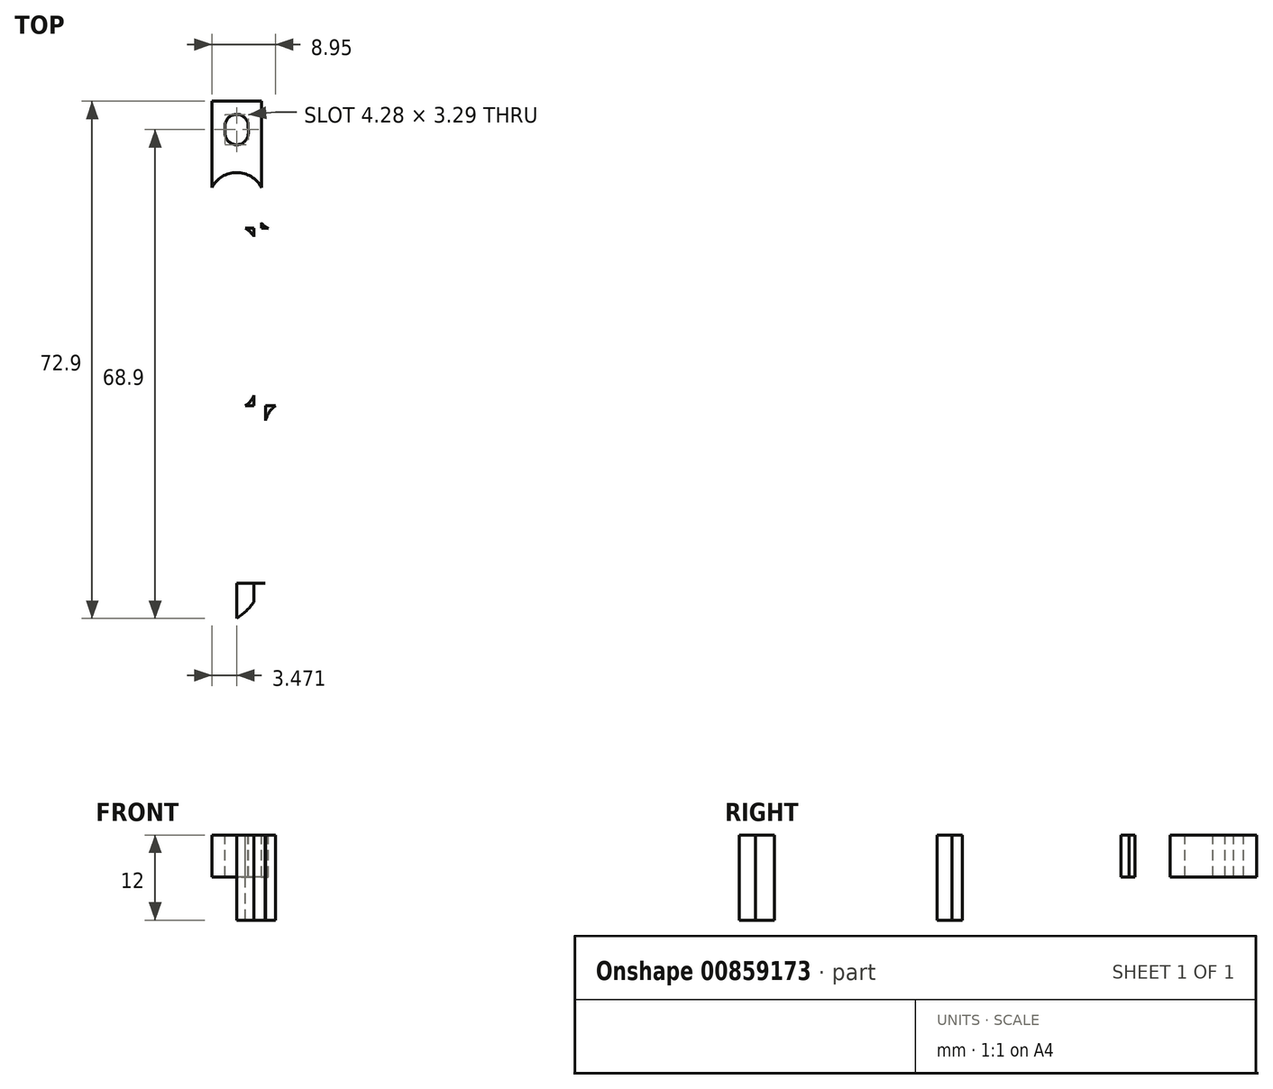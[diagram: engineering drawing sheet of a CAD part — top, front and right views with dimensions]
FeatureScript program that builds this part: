
annotation { "Feature Type Name" : "Feature", "Feature Type Description" : "" }
export const myFeature = defineFeature(function(context is Context, id is Id, definition is map)
    precondition{}
    {
        {
            var Q0;
            Q0=qCreatedBy(makeId("Top.planeOp"),FACE);
            var sketch = newSketch(context, id + "F0", { "sketchPlane" : qUnion([Q0])});
            skLineSegment(sketch, "E0.bottom", {"start": v(0, 0) * mm, "end": v(6.95, 0) * mm});
            skLineSegment(sketch, "E0.top", {"start": v(0, 17.9) * mm, "end": v(6.95, 17.9) * mm});
            skLineSegment(sketch, "E0.left", {"start": v(0, 0) * mm, "end": v(0, 17.9) * mm});
            skLineSegment(sketch, "E0.right", {"start": v(6.95, 0) * mm, "end": v(6.95, 17.9) * mm});
            skLineSegment(sketch, "E1", {"start": v(0, 0) * mm, "end": v(0, 7.85) * mm});
            skLineSegment(sketch, "E2", {"start": v(3.48, 0) * mm, "end": v(3.48, 7.85) * mm});
            skLineSegment(sketch, "E3", {"start": v(3.48, 7.85) * mm, "end": v(3.48, 6.9) * mm});
            skCircle(sketch, "E4", {"center": v(3.48, 3.92) * mm, "radius": 3.92 * mm});
            skLineSegment(sketch, "E5", {"start": v(3.47, 17.9) * mm, "end": v(3.47, 16.05) * mm});
            skLineSegment(sketch, "E6", {"start": v(3.47, 16.05) * mm, "end": v(3.48, 11.75) * mm});
            skLineSegment(sketch, "E7", {"start": v(3.47, 13.9) * mm, "end": v(3.47, 16.05) * mm});
            skLineSegment(sketch, "E8", {"start": v(3.48, 11.75) * mm, "end": v(3.47, 13.9) * mm});
            skLineSegment(sketch, "E9", {"start": v(4.55, 12.83) * mm, "end": v(4.55, 14.98) * mm});
            skLineSegment(sketch, "E10.bottom", {"start": v(3.48, 0) * mm, "end": v(1.03, 0) * mm});
            skLineSegment(sketch, "E10.top", {"start": v(3.48, -100) * mm, "end": v(1.03, -100) * mm});
            skLineSegment(sketch, "E10.left", {"start": v(3.48, 0) * mm, "end": v(3.48, -100) * mm});
            skLineSegment(sketch, "E10.right", {"start": v(1.03, 0) * mm, "end": v(1.03, -100) * mm});
            skLineSegment(sketch, "E11.bottom", {"start": v(3.48, 0) * mm, "end": v(5.93, 0) * mm});
            skLineSegment(sketch, "E11.top", {"start": v(3.48, -100) * mm, "end": v(5.93, -100) * mm});
            skLineSegment(sketch, "E11.right", {"start": v(5.93, 0) * mm, "end": v(5.93, -100) * mm});
            skLineSegment(sketch, "E12", {"start": v(5.93, 0) * mm, "end": v(5.93, 1.16) * mm});
            skLineSegment(sketch, "E13", {"start": v(1.03, 0) * mm, "end": v(1.02, 1.22) * mm});
            skLineSegment(sketch, "E14.bottom", {"start": v(6.95, 0) * mm, "end": v(9.83, -0.08) * mm});
            skLineSegment(sketch, "E14.left", {"start": v(6.95, 0) * mm, "end": v(6.95, 1.5) * mm});
            skLineSegment(sketch, "E15.right", {"start": v(5.93, -0.08) * mm, "end": v(5.93, -100) * mm});
            skLineSegment(sketch, "E16", {"start": v(3.48, 0) * mm, "end": v(3.48, -12.11) * mm});
            skLineSegment(sketch, "E17", {"start": v(3.48, 0) * mm, "end": v(3.48, -25) * mm});
            skLineSegment(sketch, "E18", {"start": v(3.48, -25) * mm, "end": v(1.03, -25) * mm});
            skLineSegment(sketch, "E19", {"start": v(1.03, -25) * mm, "end": v(1.03, -25.71) * mm});
            skLineSegment(sketch, "E20", {"start": v(1.03, -25) * mm, "end": v(1.03, -30) * mm});
            skLineSegment(sketch, "E21", {"start": v(5.93, -25) * mm, "end": v(5.93, -50) * mm});
            skPoint(sketch, "E21.startSnap0", {"position": v(2.25, -25) * mm});
            skLineSegment(sketch, "E22", {"start": v(5.93, -50) * mm, "end": v(9.83, -50.04) * mm});
            skLineSegment(sketch, "E23", {"start": v(3.48, -50) * mm, "end": v(1.03, -50) * mm});
            skLineSegment(sketch, "E24", {"start": v(5.93, -25) * mm, "end": v(9.83, -25) * mm});
            skLineSegment(sketch, "E25", {"start": v(5.93, -25) * mm, "end": v(5.93, -21.38) * mm});
            skLineSegment(sketch, "E26", {"start": v(5.93, -25) * mm, "end": v(5.93, -22.99) * mm});
            skLineSegment(sketch, "E27", {"start": v(3.48, -25) * mm, "end": v(3.48, -26.23) * mm});
            skLineSegment(sketch, "E28", {"start": v(5.93, -50) * mm, "end": v(5.93, -52.01) * mm});
            skLineSegment(sketch, "E29", {"start": v(3.48, -50) * mm, "end": v(3.48, -48.78) * mm});
            skLineSegment(sketch, "E30", {"start": v(5.93, -25) * mm, "end": v(5.93, -26.95) * mm});
            skLineSegment(sketch, "E31", {"start": v(3.48, -50) * mm, "end": v(5.93, -50) * mm});
            skLineSegment(sketch, "E32", {"start": v(3.48, 0) * mm, "end": v(3.48, -1.23) * mm});
            skLineSegment(sketch, "E33", {"start": v(6.95, 0) * mm, "end": v(6.95, 1.44) * mm});
            skLineSegment(sketch, "E34", {"start": v(1.03, 0) * mm, "end": v(1.03, -0.69) * mm});
            skLineSegment(sketch, "E35", {"start": v(1.03, 0) * mm, "end": v(1.03, -1) * mm});
            skLineSegment(sketch, "E36", {"start": v(5.92, 0) * mm, "end": v(5.92, -1.23) * mm});
            skFitSpline(sketch, "E37", {"points": [v(4.7, 0) * mm, v(5.92, -1.23) * mm], "startDerivative": vector(1.66, -0.95) * mm, "endDerivative": vector(0.86, -1.52) * mm});
            skLineSegment(sketch, "E38", {"start": v(5.93, -25) * mm, "end": v(5.93, -28.9) * mm});
            skLineSegment(sketch, "E39", {"start": v(3.48, -25) * mm, "end": v(5.93, -25) * mm});
            skLineSegment(sketch, "E40", {"start": v(5.93, -25) * mm, "end": v(5.93, -22.55) * mm});
            skLineSegment(sketch, "E41", {"start": v(5.93, -50) * mm, "end": v(5.93, -47.55) * mm});
            skLineSegment(sketch, "E42.left", {"start": v(5.93, -50) * mm, "end": v(5.93, -100) * mm});
            skLineSegment(sketch, "E43", {"start": v(9.83, -0.08) * mm, "end": v(9.83, -50.04) * mm});
            skLineSegment(sketch, "E44.bottom", {"start": v(9.83, -0.08) * mm, "end": v(12.2, -0.08) * mm});
            skLineSegment(sketch, "E44.top", {"start": v(9.83, -50.08) * mm, "end": v(12.2, -50.08) * mm});
            skLineSegment(sketch, "E44.left", {"start": v(9.83, -0.08) * mm, "end": v(9.83, -50.08) * mm});
            skLineSegment(sketch, "E44.right", {"start": v(12.2, -0.08) * mm, "end": v(12.2, -50.08) * mm});
            skLineSegment(sketch, "E45.bottom", {"start": v(5.93, -50) * mm, "end": v(8.3, -50) * mm});
            skLineSegment(sketch, "E45.top", {"start": v(5.93, -100) * mm, "end": v(8.3, -100) * mm});
            skLineSegment(sketch, "E45.right", {"start": v(8.3, -50) * mm, "end": v(8.3, -100) * mm});
            skLineSegment(sketch, "E46", {"start": v(8.3, -50) * mm, "end": v(12.2, -50.08) * mm});
            skLineSegment(sketch, "E47", {"start": v(8.3, -50) * mm, "end": v(8.3, -53.9) * mm});
            skFitSpline(sketch, "E48", {"points": [v(8.3, -53.9) * mm, v(10.24, -50.04) * mm], "startDerivative": vector(0.85, 4.55) * mm, "endDerivative": vector(3.1, 3.55) * mm});
            skLineSegment(sketch, "E49", {"start": v(3.47, 13.9) * mm, "end": v(3.47, 12.9) * mm});
            skLineSegment(sketch, "E50", {"start": v(3.47, 13.9) * mm, "end": v(3.47, 14.9) * mm});
            skCircle(sketch, "E51", {"center": v(3.47, 13.4) * mm, "radius": 1.64 * mm});
            skArc(sketch, "E52", {"start": v(5.1, 14.7) * mm, "mid": v(1.83, 14.37) * mm, "end": v(5.1, 14.14) * mm});
            skLineSegment(sketch, "E53", {"start": v(3.48, 11.75) * mm, "end": v(1.27, 11.75) * mm});
            skLineSegment(sketch, "E54", {"start": v(3.48, 11.75) * mm, "end": v(5.93, 11.75) * mm});
            skLineSegment(sketch, "E55", {"start": v(3.47, 16.05) * mm, "end": v(1.21, 16.05) * mm});
            skLineSegment(sketch, "E56", {"start": v(3.47, 16.05) * mm, "end": v(5.69, 16.05) * mm});
            skLineSegment(sketch, "E57", {"start": v(5.11, 13.43) * mm, "end": v(5.1, 14.7) * mm});
            skLineSegment(sketch, "E58", {"start": v(1.84, 13.46) * mm, "end": v(1.83, 14.38) * mm});
            skLineSegment(sketch, "E59", {"start": v(9.83, -25) * mm, "end": v(12.2, -25) * mm});
            skFitSpline(sketch, "E60", {"points": [v(11.01, -0.08) * mm, v(12.2, -1.97) * mm], "startDerivative": vector(2.1, -1.32) * mm, "endDerivative": vector(0, -2.03) * mm});
            skLineSegment(sketch, "E61", {"start": v(5.93, -25) * mm, "end": v(5.93, -43) * mm});
            skLineSegment(sketch, "E62", {"start": v(5.93, -43) * mm, "end": v(9.83, -43) * mm});
            skLineSegment(sketch, "E63", {"start": v(6.95, 0) * mm, "end": v(8.95, -0.06) * mm});
            skLineSegment(sketch, "E64", {"start": v(8.95, -0.06) * mm, "end": v(8.95, -25) * mm});
            skLineSegment(sketch, "E65", {"start": v(6.95, 0) * mm, "end": v(7.95, -0.03) * mm});
            skFitSpline(sketch, "E66", {"points": [v(7.95, -0.03) * mm, v(6.95, 0.75) * mm], "startDerivative": vector(-1.3, 0.67) * mm, "endDerivative": vector(-0.63, 0.9) * mm});
            skFitSpline(sketch, "E67", {"points": [v(7.95, -0.03) * mm, v(8.95, -1) * mm], "startDerivative": vector(1.44, -0.65) * mm, "endDerivative": vector(0.55, -1.15) * mm});
            skLineSegment(sketch, "E68", {"start": v(5.93, -25) * mm, "end": v(7.53, -25) * mm});
            skLineSegment(sketch, "E69", {"start": v(7.53, -25) * mm, "end": v(7.53, -43) * mm});
            skPoint(sketch, "E69.endSnap0", {"position": v(7.88, -43) * mm});
            skFitSpline(sketch, "E70", {"points": [v(8.95, -25) * mm, v(7.53, -27.1) * mm], "startDerivative": vector(-2.11, -1.57) * mm, "endDerivative": vector(-1.16, -3.2) * mm});
            skCircle(sketch, "E71", {"center": v(3.48, 3.92) * mm, "radius": 2.77 * mm});
            skFitSpline(sketch, "E72", {"points": [v(4.7, -25) * mm, v(5.93, -23.52) * mm], "startDerivative": vector(1.9, 1.19) * mm, "endDerivative": vector(0.85, 2) * mm});
            skFitSpline(sketch, "E73", {"points": [v(4.7, -25) * mm, v(3.48, -26.23) * mm], "startDerivative": vector(-1.92, -0.79) * mm, "endDerivative": vector(-0.51, -1.86) * mm});
            skLineSegment(sketch, "E74", {"start": v(7.53, -43) * mm, "end": v(7.45, -50.02) * mm});
            skLineSegment(sketch, "E75", {"start": v(3.48, -50) * mm, "end": v(3.48, -55) * mm});
            skLineSegment(sketch, "E76", {"start": v(3.48, -55) * mm, "end": v(7.45, -55) * mm});
            skLineSegment(sketch, "E77", {"start": v(7.45, -55) * mm, "end": v(7.45, -50.02) * mm});
            skFitSpline(sketch, "E78", {"points": [v(3.48, -55) * mm, v(7.45, -50.02) * mm], "startDerivative": vector(6.1, 4.07) * mm, "endDerivative": vector(2.72, 5.79) * mm});
            skSolve(sketch);
        }
        {
            var Q0;
            {var subQ0=sQuery(id+"F0.wireOp",EDGE,"E4");var subQ3=sQuery(id+"F0.wireOp",EDGE,"E0.right");var subQ10=makeQuery(id+"F0.imprint","INTERSECT",VERTEX,{"disambiguationData":[OD(0.0)],"derivedFrom":[subQ3,subQ0]});Q0=makeQuery(id+"F0.imprint","IMPRINT",FACE,{"disambiguationData":[TD([[makeQuery(id+"F0.imprint","IMPRINT",EDGE,{"disambiguationData":[TD([[subQ10,-1.0]])],"derivedFrom":subQ3}),1.0]])]});}
            var Q1;
            {var subQ0=sQuery(id+"F0.wireOp",EDGE,"E4");var subQ7=sQuery(id+"F0.wireOp",EDGE,"E1");var subQ10=makeQuery(id+"F0.imprint","INTERSECT",VERTEX,{"disambiguationData":[OD(0.0)],"derivedFrom":[subQ7,subQ0]});Q1=makeQuery(id+"F0.imprint","IMPRINT",FACE,{"disambiguationData":[TD([[makeQuery(id+"F0.imprint","IMPRINT",EDGE,{"disambiguationData":[TD([[subQ10,-1.0]])],"derivedFrom":subQ7}),-1.0]])]});}
            var Q2;
            {var subQ0=sQuery(id+"F0.wireOp",EDGE,"E1");var subQ1=sQuery(id+"F0.wireOp",EDGE,"E0.bottom");var subQ2=makeQuery(id+"F0.imprint","INTERSECT",VERTEX,{"derivedFrom":[subQ1,subQ0]});Q2=makeQuery(id+"F0.imprint","IMPRINT",FACE,{"disambiguationData":[TD([[makeQuery(id+"F0.imprint","IMPRINT",EDGE,{"disambiguationData":[TD([[subQ2,-1.0]])],"derivedFrom":subQ0}),-1.0]])]});}
            var Q3;
            {var subQ0=sQuery(id+"F0.wireOp",EDGE,"E10.bottom");Q3=makeQuery(id+"F0.imprint","IMPRINT",FACE,{"disambiguationData":[TD([[makeQuery(id+"F0.imprint","IMPRINT",EDGE,{"derivedFrom":subQ0}),-1.0]])]});}
            var Q4;
            {var subQ0=sQuery(id+"F0.wireOp",EDGE,"E4");var subQ1=sQuery(id+"F0.wireOp",EDGE,"E1");var subQ2=makeQuery(id+"F0.imprint","INTERSECT",VERTEX,{"disambiguationData":[OD(0.0)],"derivedFrom":[subQ1,subQ0]});Q4=makeQuery(id+"F0.imprint","IMPRINT",FACE,{"disambiguationData":[TD([[makeQuery(id+"F0.imprint","IMPRINT",EDGE,{"disambiguationData":[TD([[subQ2,-1.0]])],"derivedFrom":subQ1}),1.0]])]});}
            var Q5;
            {var subQ0=sQuery(id+"F0.wireOp",EDGE,"E4");var subQ1=sQuery(id+"F0.wireOp",EDGE,"E0.right");var subQ2=makeQuery(id+"F0.imprint","INTERSECT",VERTEX,{"disambiguationData":[OD(0.0)],"derivedFrom":[subQ1,subQ0]});Q5=makeQuery(id+"F0.imprint","IMPRINT",FACE,{"disambiguationData":[TD([[makeQuery(id+"F0.imprint","IMPRINT",EDGE,{"disambiguationData":[TD([[subQ2,-1.0]])],"derivedFrom":subQ1}),-1.0]])]});}
            var Q6;
            {var subQ5=sQuery(id+"F0.wireOp",EDGE,"E14.left");Q6=makeQuery(id+"F0.imprint","IMPRINT",FACE,{"disambiguationData":[TD([[makeQuery(id+"F0.imprint","IMPRINT",EDGE,{"derivedFrom":subQ5}),1.0]])]});}
            var Q7;
            {var subQ0=sQuery(id+"F0.wireOp",EDGE,"E11.bottom");var subQ5=makeQuery(id+"F0.imprint","INTERSECT",VERTEX,{"derivedFrom":[subQ0,sQuery(id+"F0.wireOp",EDGE,"E37")]});Q7=makeQuery(id+"F0.imprint","IMPRINT",FACE,{"disambiguationData":[TD([[makeQuery(id+"F0.imprint","IMPRINT",EDGE,{"disambiguationData":[TD([[subQ5,-1.0]])],"derivedFrom":subQ0}),1.0]])]});}
            var Q8;
            {var subQ3=sQuery(id+"F0.wireOp",EDGE,"E37");Q8=makeQuery(id+"F0.imprint","IMPRINT",FACE,{"disambiguationData":[TD([[makeQuery(id+"F0.imprint","IMPRINT",EDGE,{"derivedFrom":subQ3}),1.0]])]});}
            var Q9;
            Q9=makeQuery(id+"F0.imprint","IMPRINT",FACE,{"disambiguationData":[TD([[makeQuery(id+"F0.imprint","IMPRINT",EDGE,{"derivedFrom":sQuery(id+"F0.wireOp",EDGE,"E14.bottom")}),1.0]])]});
            extrude(context, id + "F1", {"entities" : qUnion([Q0, Q1, Q2, Q3, Q4, Q5, Q6, Q7, Q8, Q9]), "depth" : -5.9 * mm, "offsetDistance" : 25 * mm});
        }
        {
            var Q0;
            {var subQ15=sQuery(id+"F0.wireOp",EDGE,"E0.left");Q0=makeQuery(id+"F0.imprint","IMPRINT",FACE,{"disambiguationData":[TD([[makeQuery(id+"F0.imprint","IMPRINT",EDGE,{"derivedFrom":subQ15}),-1.0]])]});}
            extrude(context, id + "F2", {"entities" : qUnion([Q0]), "operationType" : NewBodyOperationType.ADD, "depth" : -2.5 * mm, "offsetDistance" : 25 * mm});
        }
        {
            var Q0;
            {var subQ5=sQuery(id+"F0.wireOp",EDGE,"E31");Q0=makeQuery(id+"F0.imprint","IMPRINT",FACE,{"disambiguationData":[TD([[makeQuery(id+"F0.imprint","IMPRINT",EDGE,{"derivedFrom":subQ5}),-1.0]])]});}
            var Q1;
            {var subQ0=sQuery(id+"F0.wireOp",EDGE,"E42.left");var subQ5=makeQuery(id+"F0.imprint","IMPRINT",VERTEX,{"derivedFrom":subQ0});Q1=makeQuery(id+"F0.imprint","IMPRINT",FACE,{"disambiguationData":[TD([[makeQuery(id+"F0.imprint","IMPRINT",EDGE,{"disambiguationData":[TD([[subQ5,-1.0]])],"derivedFrom":subQ0}),1.0]])]});}
            var Q2;
            {var subQ6=sQuery(id+"F0.wireOp",EDGE,"E21");Q2=makeQuery(id+"F0.imprint","IMPRINT",FACE,{"disambiguationData":[TD([[makeQuery(id+"F0.imprint","IMPRINT",EDGE,{"derivedFrom":subQ6}),1.0]])]});}
            var Q3;
            {var subQ6=sQuery(id+"F0.wireOp",EDGE,"E21");Q3=makeQuery(id+"F0.imprint","IMPRINT",FACE,{"disambiguationData":[TD([[makeQuery(id+"F0.imprint","IMPRINT",EDGE,{"derivedFrom":subQ6}),-1.0]])]});}
            var Q4;
            {var subQ8=sQuery(id+"F0.wireOp",EDGE,"E68");Q4=makeQuery(id+"F0.imprint","IMPRINT",FACE,{"disambiguationData":[TD([[makeQuery(id+"F0.imprint","IMPRINT",EDGE,{"derivedFrom":subQ8}),-1.0]])]});}
            var Q5;
            {var subQ4=sQuery(id+"F0.wireOp",EDGE,"E15.right");Q5=makeQuery(id+"F0.imprint","IMPRINT",FACE,{"disambiguationData":[TD([[makeQuery(id+"F0.imprint","IMPRINT",EDGE,{"derivedFrom":subQ4}),1.0]])]});}
            var Q6;
            {var subQ3=sQuery(id+"F0.wireOp",EDGE,"E72");Q6=makeQuery(id+"F0.imprint","IMPRINT",FACE,{"disambiguationData":[TD([[makeQuery(id+"F0.imprint","IMPRINT",EDGE,{"derivedFrom":subQ3}),-1.0]])]});}
            var Q7;
            {var subQ3=sQuery(id+"F0.wireOp",EDGE,"E70");Q7=makeQuery(id+"F0.imprint","IMPRINT",FACE,{"disambiguationData":[TD([[makeQuery(id+"F0.imprint","IMPRINT",EDGE,{"derivedFrom":subQ3}),-1.0]])]});}
            extrude(context, id + "F3", {"entities" : qUnion([Q0, Q1, Q2, Q3, Q4, Q5, Q6, Q7]), "operationType" : NewBodyOperationType.ADD, "depth" : -12 * mm, "offsetDistance" : 25 * mm});
        }
        {
            var Q0;
            {var subQ0=sQuery(id+"F0.wireOp",EDGE,"E45.bottom");var subQ3=sQuery(id+"F0.wireOp",EDGE,"E74");var subQ5=makeQuery(id+"F0.imprint","INTERSECT",VERTEX,{"derivedFrom":[subQ0,subQ3]});Q0=makeQuery(id+"F0.imprint","IMPRINT",FACE,{"disambiguationData":[TD([[makeQuery(id+"F0.imprint","IMPRINT",EDGE,{"disambiguationData":[TD([[subQ5,-1.0]])],"derivedFrom":subQ3}),-1.0]])]});}
            extrude(context, id + "F4", {"entities" : qUnion([Q0]), "operationType" : NewBodyOperationType.ADD, "depth" : -12 * mm, "offsetDistance" : 25 * mm});
        }
    });
